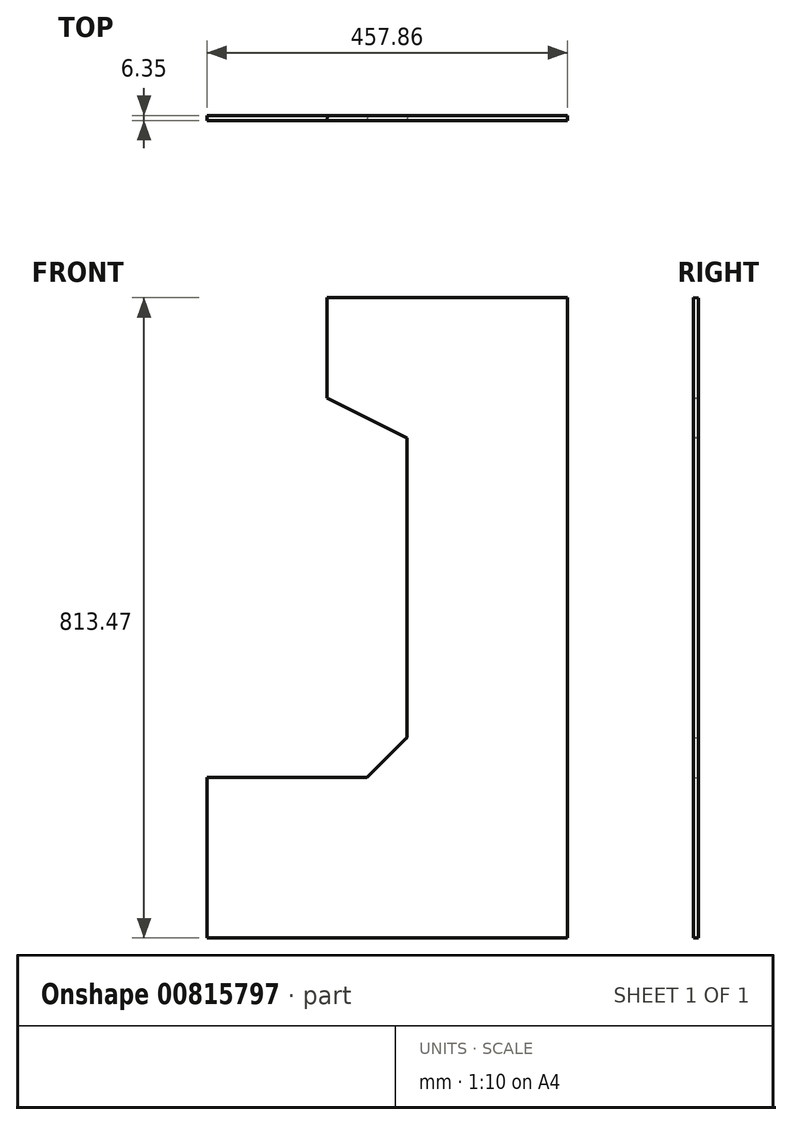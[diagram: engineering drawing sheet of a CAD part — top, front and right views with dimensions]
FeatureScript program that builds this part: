
annotation { "Feature Type Name" : "Feature", "Feature Type Description" : "" }
export const myFeature = defineFeature(function(context is Context, id is Id, definition is map)
    precondition{}
    {
        {
            var Q0;
            Q0=qCreatedBy(makeId("Front.planeOp"),FACE);
            var sketch = newSketch(context, id + "F0", { "sketchPlane" : qUnion([Q0])});
            skLineSegment(sketch, "E0", {"start": v(-152.4, -152.19) * mm, "end": v(-152.4, -355.39) * mm});
            skLineSegment(sketch, "E1", {"start": v(-152.4, -355.39) * mm, "end": v(304.8, -355.39) * mm});
            skLineSegment(sketch, "E2", {"start": v(304.8, -355.39) * mm, "end": v(304.8, 457.41) * mm});
            skLineSegment(sketch, "E3", {"start": v(304.8, 457.41) * mm, "end": v(0, 457.41) * mm});
            skLineSegment(sketch, "E4", {"start": v(0, 457.41) * mm, "end": v(0, 330.41) * mm});
            skLineSegment(sketch, "E5", {"start": v(0, 330.41) * mm, "end": v(101.6, 279.61) * mm});
            skLineSegment(sketch, "E6", {"start": v(101.6, -101.39) * mm, "end": v(101.6, 279.61) * mm});
            skLineSegment(sketch, "E7", {"start": v(50.8, -152.19) * mm, "end": v(-152.4, -152.19) * mm});
            skLineSegment(sketch, "E8", {"start": v(50.8, -152.19) * mm, "end": v(101.6, -101.39) * mm});
            skPoint(sketch, "E9.orphan", {"position": v(101.6, -152.19) * mm});
            skSolve(sketch);
        }
        {
            var Q0;
            Q0 = qSketchRegion(id + "F0", true);
            extrude(context, id + "F1", {"entities" : qUnion([Q0]), "depth" : 6.35 * mm, "offsetDistance" : 25.4 * mm, "hasDraft" : true, "draftAngle" : 3 * degree});
        }
    });
